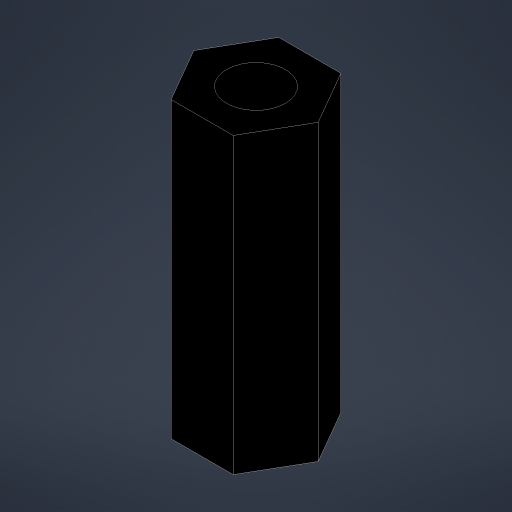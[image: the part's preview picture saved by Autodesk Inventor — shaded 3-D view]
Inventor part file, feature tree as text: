
AUTODESK INVENTOR PART (.ipt)
format: ipt  version: 2025 (Build 290162010, 162A)  size: 162,304 bytes
history: native  units: mm
features: extrude x1, sketch x1
ambient origin geometry x8: Origin, YZ Plane, XZ Plane, XY Plane, X Axis, Y Axis, Z Axis, Center Point
bodies: Solid1 (feature_tree)
feature tree (2):
  extrude  "Extrusion1"  Depth=15.0mm
  sketch  "Sketch1"  dims[d0=5.5mm d1=3.0mm d2=15.0mm d3=0.0mm d4=0.5mm d5=0.872665mm]
